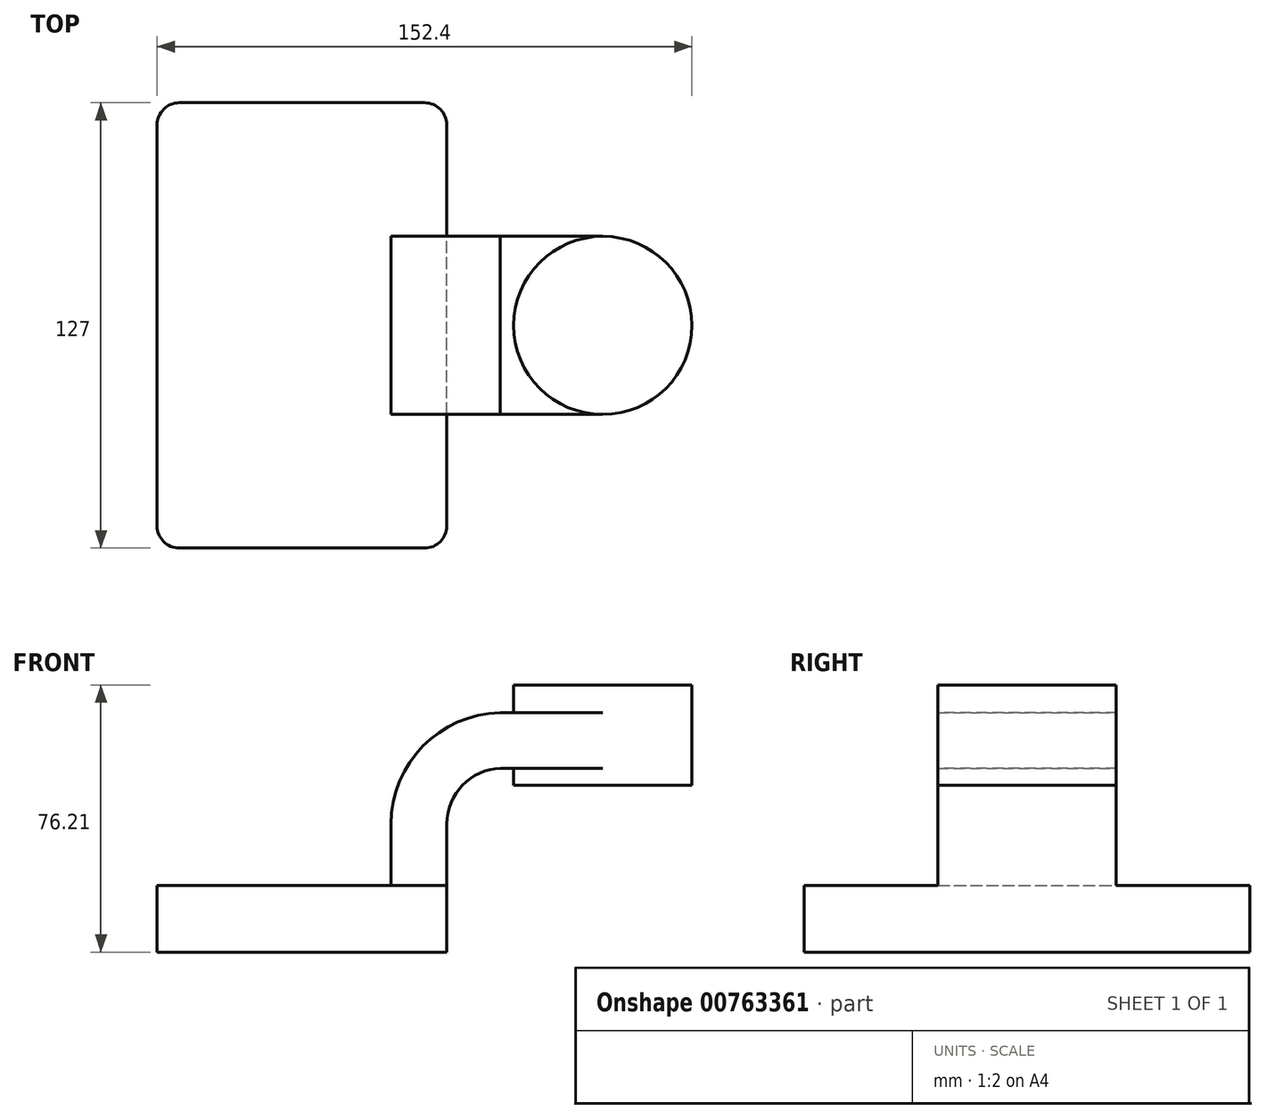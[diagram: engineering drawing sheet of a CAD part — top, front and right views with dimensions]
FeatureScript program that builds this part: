
annotation { "Feature Type Name" : "Feature", "Feature Type Description" : "" }
export const myFeature = defineFeature(function(context is Context, id is Id, definition is map)
    precondition{}
    {
        {
            var Q0;
            Q0=qCreatedBy(makeId("Front.planeOp"),FACE);
            var sketch = newSketch(context, id + "F0", { "sketchPlane" : qUnion([Q0])});
            skLineSegment(sketch, "E0.bottom", {"start": v(41.27, 9.53) * mm, "end": v(-41.28, 9.53) * mm});
            skLineSegment(sketch, "E0.top", {"start": v(41.28, -9.52) * mm, "end": v(-41.27, -9.52) * mm});
            skLineSegment(sketch, "E0.left", {"start": v(41.28, 9.53) * mm, "end": v(41.28, -9.52) * mm});
            skLineSegment(sketch, "E0.right", {"start": v(-41.28, 9.53) * mm, "end": v(-41.27, -9.52) * mm});
            skPoint(sketch, "E0.middle", {"position": v(0, 0) * mm});
            skLineSegment(sketch, "E1.bottom", {"start": v(111.12, 38.1) * mm, "end": v(60.32, 38.1) * mm});
            skLineSegment(sketch, "E1.top", {"start": v(111.12, 66.68) * mm, "end": v(60.32, 66.68) * mm});
            skLineSegment(sketch, "E1.left", {"start": v(111.12, 38.1) * mm, "end": v(111.12, 66.68) * mm});
            skLineSegment(sketch, "E1.right", {"start": v(60.32, 38.1) * mm, "end": v(60.32, 66.68) * mm});
            skLineSegment(sketch, "E2", {"start": v(41.27, 9.53) * mm, "end": v(41.27, 27) * mm});
            skArc(sketch, "E3", {"start": v(41.27, 27) * mm, "mid": v(45.75, 38.05) * mm, "end": v(56.65, 42.88) * mm});
            skLineSegment(sketch, "E4", {"start": v(56.65, 42.88) * mm, "end": v(85.72, 42.88) * mm});
            skLineSegment(sketch, "E5.0", {"start": v(56.44, 58.75) * mm, "end": v(85.72, 58.75) * mm});
            skArc(sketch, "E5.1", {"start": v(25.4, 27) * mm, "mid": v(34.45, 49.2) * mm, "end": v(56.44, 58.75) * mm});
            skLineSegment(sketch, "E5.2", {"start": v(25.4, 9.53) * mm, "end": v(25.4, 27) * mm});
            skFitSpline(sketch, "E6", {"points": [v(-41.28, 9.53) * mm, v(56.44, 58.75) * mm], "startDerivative": vector(0.5, 96.78) * mm, "endDerivative": vector(169.32, 1.38) * mm});
            skLineSegment(sketch, "E7", {"start": v(85.72, 66.68) * mm, "end": v(85.72, 38.1) * mm});
            skSolve(sketch);
        }
        {
            var Q0;
            Q0=makeQuery(id+"F0.imprint","IMPRINT",FACE,{"disambiguationData":[TD([[makeQuery(id+"F0.imprint","IMPRINT",EDGE,{"derivedFrom":sQuery(id+"F0.wireOp",EDGE,"E0.top")}),-1.0]])]});
            extrude(context, id + "F1", {"entities" : qUnion([Q0]), "endBound" : BoundingType.SYMMETRIC, "depth" : 127 * mm, "offsetDistance" : 25.4 * mm});
        }
        {
            var Q0;
            {var subQ1=sQuery(id+"F0.wireOp",EDGE,"E2");Q0=makeQuery(id+"F0.imprint","IMPRINT",FACE,{"disambiguationData":[TD([[makeQuery(id+"F0.imprint","IMPRINT",EDGE,{"derivedFrom":subQ1}),1.0]])]});}
            var Q1;
            {var subQ0=sQuery(id+"F0.wireOp",EDGE,"E4");var subQ1=sQuery(id+"F0.wireOp",EDGE,"E1.right");var subQ2=makeQuery(id+"F0.imprint","INTERSECT",VERTEX,{"derivedFrom":[subQ1,subQ0]});Q1=makeQuery(id+"F0.imprint","IMPRINT",FACE,{"disambiguationData":[TD([[makeQuery(id+"F0.imprint","IMPRINT",EDGE,{"disambiguationData":[TD([[subQ2,-1.0]])],"derivedFrom":subQ1}),-1.0]])]});}
            extrude(context, id + "F2", {"entities" : qUnion([Q0, Q1]), "operationType" : NewBodyOperationType.ADD, "endBound" : BoundingType.SYMMETRIC, "depth" : 50.8 * mm, "offsetDistance" : 25.4 * mm});
        }
        {
            var Q0;
            Q0=makeQuery(id+"F0.imprint","IMPRINT",FACE,{"disambiguationData":[TD([[makeQuery(id+"F0.imprint","IMPRINT",EDGE,{"derivedFrom":sQuery(id+"F0.wireOp",EDGE,"E5.1")}),1.0]])]});
            extrude(context, id + "F3", {"entities" : qUnion([Q0]), "operationType" : NewBodyOperationType.ADD, "endBound" : BoundingType.SYMMETRIC, "depth" : 16.5 * mm, "offsetDistance" : 25.4 * mm});
        }
        {
            var Q0;
            {var subQ0=sQuery(id+"F0.wireOp",EDGE,"E1.left");Q0=makeQuery(id+"F0.imprint","IMPRINT",FACE,{"disambiguationData":[TD([[makeQuery(id+"F0.imprint","IMPRINT",EDGE,{"derivedFrom":subQ0}),1.0]])]});}
            var Q1;
            Q1=sQuery(id+"F0.wireOp",EDGE,"E7");
            revolve(context, id + "F4", {"operationType" : NewBodyOperationType.ADD, "surfaceOperationType" : NewSurfaceOperationType.NEW, "entities" : qUnion([Q0]), "axis" : qUnion([Q1]), "revolveType" : RevolveType.FULL});
        }
        {
            var Q0;
            Q0=makeQuery(id+"F1.opExtrude","CAP_EDGE",EDGE,{"disambiguationData":[OSD([sQuery(id+"F0.wireOp",EDGE,"E0.left")])],"isStart":true});
            var Q1;
            Q1=makeQuery(id+"F1.opExtrude","CAP_EDGE",EDGE,{"disambiguationData":[OSD([sQuery(id+"F0.wireOp",EDGE,"E0.right")])],"isStart":true});
            var Q2;
            Q2=makeQuery(id+"F1.opExtrude","CAP_EDGE",EDGE,{"disambiguationData":[OSD([sQuery(id+"F0.wireOp",EDGE,"E0.right")])],"isStart":false});
            var Q3;
            Q3=makeQuery(id+"F1.opExtrude","CAP_EDGE",EDGE,{"disambiguationData":[OSD([sQuery(id+"F0.wireOp",EDGE,"E0.left")])],"isStart":false});
            fillet(context, id + "F5", {"entities" : qUnion([Q0, Q1, Q2, Q3]), "radius" : 6.35 * mm, "tangentPropagation" : true, "allowEdgeOverflow" : false});
        }
    });
